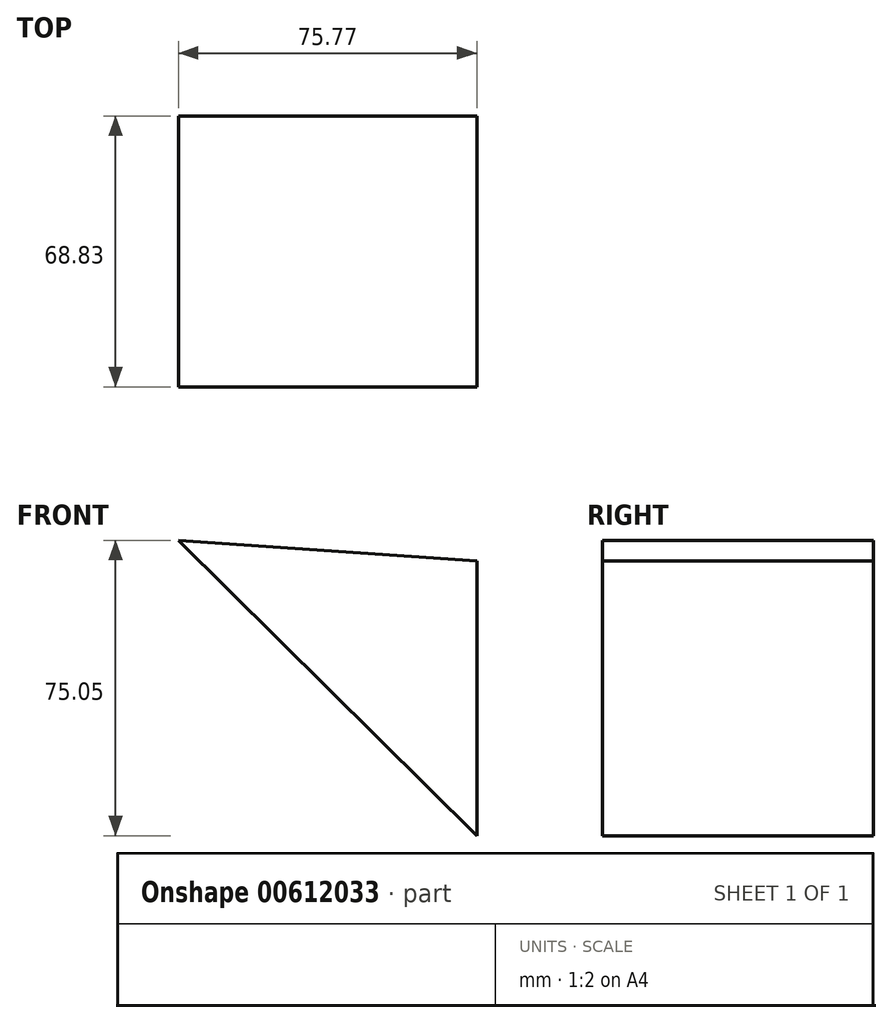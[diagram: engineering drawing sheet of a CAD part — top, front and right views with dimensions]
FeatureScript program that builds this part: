
annotation { "Feature Type Name" : "Feature", "Feature Type Description" : "" }
export const myFeature = defineFeature(function(context is Context, id is Id, definition is map)
    precondition{}
    {
        {
            var Q0;
            Q0=qCreatedBy(makeId("Front.planeOp"),FACE);
            var sketch = newSketch(context, id + "F0", { "sketchPlane" : qUnion([Q0])});
            skLineSegment(sketch, "E0", {"start": v(75.77, -75.05) * mm, "end": v(75.77, -5.24) * mm});
            skLineSegment(sketch, "E1", {"start": v(75.77, -5.24) * mm, "end": v(0, 0) * mm});
            skLineSegment(sketch, "E2", {"start": v(0, 0) * mm, "end": v(75.77, -75.05) * mm});
            skSolve(sketch);
        }
        {
            var Q0;
            Q0 = qSketchRegion(id + "F0", true);
            extrude(context, id + "F1", {"entities" : qUnion([Q0]), "depth" : 68.83 * mm, "offsetDistance" : 25.4 * mm});
        }
    });
